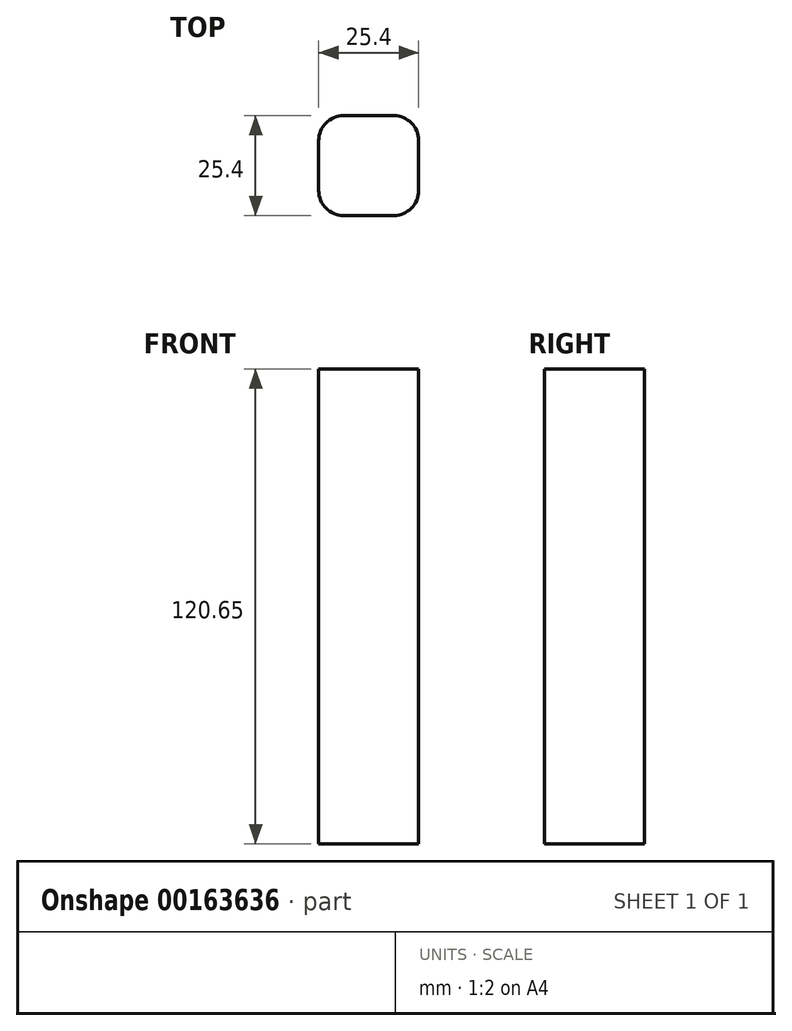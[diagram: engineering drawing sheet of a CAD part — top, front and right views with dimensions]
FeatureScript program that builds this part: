
annotation { "Feature Type Name" : "Feature", "Feature Type Description" : "" }
export const myFeature = defineFeature(function(context is Context, id is Id, definition is map)
    precondition{}
    {
        {
            var Q0;
            Q0=qCreatedBy(makeId("Top.planeOp"),FACE);
            var sketch = newSketch(context, id + "F0", { "sketchPlane" : qUnion([Q0])});
            skLineSegment(sketch, "E0.bottom", {"start": v(6.35, 12.7) * mm, "end": v(-6.35, 12.7) * mm});
            skLineSegment(sketch, "E0.top", {"start": v(6.35, -12.7) * mm, "end": v(-6.35, -12.7) * mm});
            skLineSegment(sketch, "E0.left", {"start": v(12.7, 6.35) * mm, "end": v(12.7, -6.35) * mm});
            skLineSegment(sketch, "E0.right", {"start": v(-12.7, 6.35) * mm, "end": v(-12.7, -6.35) * mm});
            skPoint(sketch, "E0.middle", {"position": v(0, 0) * mm});
            skPoint(sketch, "E1.visualSharp", {"position": v(-12.7, 12.7) * mm});
            skArc(sketch, "E1.filletArc", {"start": v(-6.35, 12.7) * mm, "mid": v(-10.84, 10.84) * mm, "end": v(-12.7, 6.35) * mm});
            skPoint(sketch, "E2.visualSharp", {"position": v(-12.7, -12.7) * mm});
            skArc(sketch, "E2.filletArc", {"start": v(-12.7, -6.35) * mm, "mid": v(-10.84, -10.84) * mm, "end": v(-6.35, -12.7) * mm});
            skPoint(sketch, "E3.visualSharp", {"position": v(12.7, -12.7) * mm});
            skArc(sketch, "E3.filletArc", {"start": v(6.35, -12.7) * mm, "mid": v(10.84, -10.84) * mm, "end": v(12.7, -6.35) * mm});
            skPoint(sketch, "E4.visualSharp", {"position": v(12.7, 12.7) * mm});
            skArc(sketch, "E4.filletArc", {"start": v(12.7, 6.35) * mm, "mid": v(10.84, 10.84) * mm, "end": v(6.35, 12.7) * mm});
            skSolve(sketch);
        }
        {
            var Q0;
            Q0=qSketchRegion(id+"F0",true);
            extrude(context, id + "F1", {"entities" : qUnion([Q0]), "depth" : 120.65 * mm, "offsetDistance" : 25.4 * mm});
        }
    });
